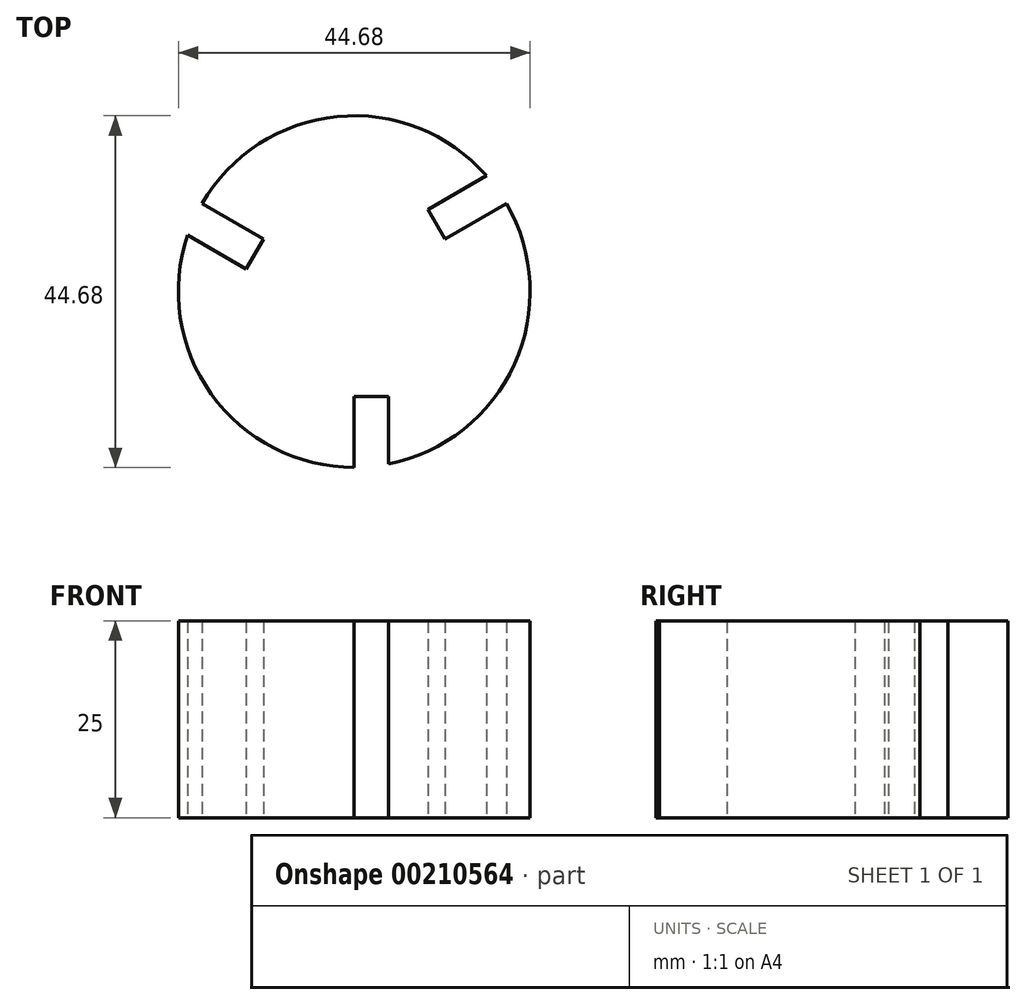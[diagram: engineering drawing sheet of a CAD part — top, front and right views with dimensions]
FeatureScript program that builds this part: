
annotation { "Feature Type Name" : "Feature", "Feature Type Description" : "" }
export const myFeature = defineFeature(function(context is Context, id is Id, definition is map)
    precondition{}
    {
        {
            var Q0;
            Q0=qCreatedBy(makeId("Top.planeOp"),FACE);
            var sketch = newSketch(context, id + "F0", { "sketchPlane" : qUnion([Q0])});
            skCircle(sketch, "E0", {"center": v(0, 0) * mm, "radius": 22.34 * mm});
            skLineSegment(sketch, "E1.bottom", {"start": v(0, -13.34) * mm, "end": v(4.37, -13.34) * mm});
            skLineSegment(sketch, "E1.top", {"start": v(0, -39.05) * mm, "end": v(4.37, -39.05) * mm});
            skLineSegment(sketch, "E1.left", {"start": v(0, -13.34) * mm, "end": v(0, -39.05) * mm});
            skLineSegment(sketch, "E1.right", {"start": v(4.37, -13.34) * mm, "end": v(4.37, -39.05) * mm});
            skLineSegment(sketch, "E2.1.0", {"start": v(9.37, 10.45) * mm, "end": v(31.63, 23.3) * mm});
            skLineSegment(sketch, "E2.1.1", {"start": v(11.55, 6.67) * mm, "end": v(33.81, 19.52) * mm});
            skLineSegment(sketch, "E2.1.2", {"start": v(33.81, 19.52) * mm, "end": v(31.63, 23.3) * mm});
            skLineSegment(sketch, "E2.1.3", {"start": v(11.55, 6.67) * mm, "end": v(9.37, 10.45) * mm});
            skLineSegment(sketch, "E2.2.0", {"start": v(-13.73, 2.89) * mm, "end": v(-36, 15.74) * mm});
            skLineSegment(sketch, "E2.2.1", {"start": v(-11.55, 6.67) * mm, "end": v(-33.81, 19.52) * mm});
            skLineSegment(sketch, "E2.2.2", {"start": v(-33.81, 19.52) * mm, "end": v(-36, 15.74) * mm});
            skLineSegment(sketch, "E2.2.3", {"start": v(-11.55, 6.67) * mm, "end": v(-13.73, 2.89) * mm});
            skSolve(sketch);
        }
        {
            var Q0;
            {var subQ8=sQuery(id+"F0.wireOp",EDGE,"E1.bottom");Q0=makeQuery(id+"F0.imprint","IMPRINT",FACE,{"disambiguationData":[TD([[makeQuery(id+"F0.imprint","IMPRINT",EDGE,{"derivedFrom":subQ8}),1.0]])]});}
            extrude(context, id + "F1", {"entities" : qUnion([Q0]), "depth" : 25 * mm});
        }
    });
